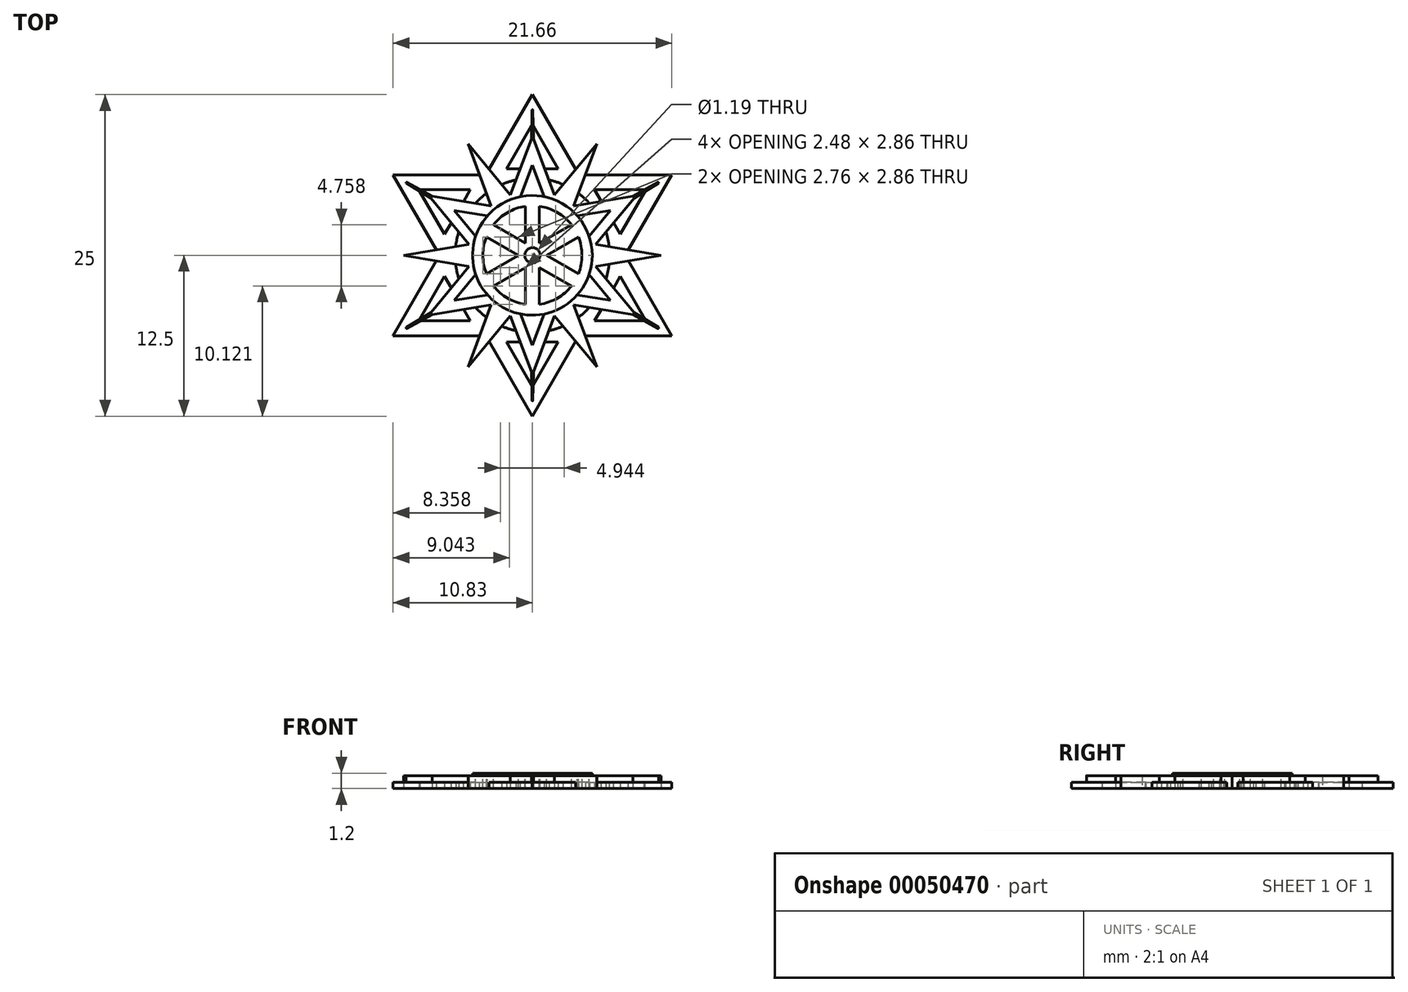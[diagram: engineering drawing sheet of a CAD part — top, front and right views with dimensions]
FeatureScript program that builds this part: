
annotation { "Feature Type Name" : "Feature", "Feature Type Description" : "" }
export const myFeature = defineFeature(function(context is Context, id is Id, definition is map)
    precondition{}
    {
        {
            var Q0;
            Q0=qCreatedBy(makeId("Top.planeOp"),FACE);
            var sketch = newSketch(context, id + "F0", { "sketchPlane" : qUnion([Q0])});
            skCircle(sketch, "E0", {"center": v(0, 0) * mm, "radius": 12.5 * mm, "construction": true});
            skLineSegment(sketch, "E1", {"start": v(0, 12.5) * mm, "end": v(-10.83, -6.25) * mm});
            skLineSegment(sketch, "E2", {"start": v(-10.83, -6.25) * mm, "end": v(10.83, -6.25) * mm});
            skLineSegment(sketch, "E3", {"start": v(10.83, -6.25) * mm, "end": v(0, 12.5) * mm});
            skLineSegment(sketch, "E4", {"start": v(-10.83, 6.25) * mm, "end": v(10.83, 6.25) * mm});
            skLineSegment(sketch, "E5", {"start": v(10.83, 6.25) * mm, "end": v(0, -12.5) * mm});
            skLineSegment(sketch, "E6", {"start": v(0, -12.5) * mm, "end": v(-10.83, 6.25) * mm});
            skCircle(sketch, "E7", {"center": v(0, 0) * mm, "radius": 6 * mm});
            skLineSegment(sketch, "E8", {"start": v(-2, 6.73) * mm, "end": v(2, 6.73) * mm});
            skLineSegment(sketch, "E9", {"start": v(2, 6.73) * mm, "end": v(0, 10.2) * mm});
            skLineSegment(sketch, "E10", {"start": v(0, 10.2) * mm, "end": v(-2, 6.73) * mm});
            skLineSegment(sketch, "E11", {"start": v(0, 10.2) * mm, "end": v(0, 12.5) * mm, "construction": true});
            skLineSegment(sketch, "E12.1.0", {"start": v(-4.83, 5.1) * mm, "end": v(-8.83, 5.1) * mm});
            skLineSegment(sketch, "E12.1.1", {"start": v(-6.83, 1.63) * mm, "end": v(-4.83, 5.1) * mm});
            skLineSegment(sketch, "E12.1.2", {"start": v(-8.83, 5.1) * mm, "end": v(-6.83, 1.63) * mm});
            skLineSegment(sketch, "E12.2.0", {"start": v(-6.83, -1.63) * mm, "end": v(-8.83, -5.1) * mm});
            skLineSegment(sketch, "E12.2.1", {"start": v(-4.83, -5.1) * mm, "end": v(-6.83, -1.63) * mm});
            skLineSegment(sketch, "E12.2.2", {"start": v(-8.83, -5.1) * mm, "end": v(-4.83, -5.1) * mm});
            skLineSegment(sketch, "E12.3.0", {"start": v(-2, -6.73) * mm, "end": v(0, -10.2) * mm});
            skLineSegment(sketch, "E12.3.1", {"start": v(2, -6.73) * mm, "end": v(-2, -6.73) * mm});
            skLineSegment(sketch, "E12.3.2", {"start": v(0, -10.2) * mm, "end": v(2, -6.73) * mm});
            skLineSegment(sketch, "E12.4.0", {"start": v(4.83, -5.1) * mm, "end": v(8.83, -5.1) * mm});
            skLineSegment(sketch, "E12.4.1", {"start": v(6.83, -1.63) * mm, "end": v(4.83, -5.1) * mm});
            skLineSegment(sketch, "E12.4.2", {"start": v(8.83, -5.1) * mm, "end": v(6.83, -1.63) * mm});
            skLineSegment(sketch, "E12.5.0", {"start": v(6.83, 1.63) * mm, "end": v(8.83, 5.1) * mm});
            skLineSegment(sketch, "E12.5.1", {"start": v(4.83, 5.1) * mm, "end": v(6.83, 1.63) * mm});
            skLineSegment(sketch, "E12.5.2", {"start": v(8.83, 5.1) * mm, "end": v(4.83, 5.1) * mm});
            skSolve(sketch);
        }
        {
            var Q0;
            Q0=qSketchRegion(id+"F0",true);
            extrude(context, id + "F1", {"entities" : qUnion([Q0]), "depth" : .5 * mm});
        }
        {
            var Q0;
            Q0=qCreatedBy(makeId("Top.planeOp"),FACE);
            var sketch = newSketch(context, id + "F2", { "sketchPlane" : qUnion([Q0])});
            skArc(sketch, "E13", {"start": v(-1.72, 4.7) * mm, "mid": v(-2.5, 4.33) * mm, "end": v(-3.2, 3.84) * mm});
            skLineSegment(sketch, "E14", {"start": v(-1.72, 4.7) * mm, "end": v(-0.08, 9.05) * mm});
            skLineSegment(sketch, "E15", {"start": v(0.08, 9.05) * mm, "end": v(1.72, 4.7) * mm});
            skLineSegment(sketch, "E16", {"start": v(-0.08, 9.05) * mm, "end": v(-0.04, 11.28) * mm});
            skLineSegment(sketch, "E17", {"start": v(0.04, 11.28) * mm, "end": v(0.08, 9.05) * mm});
            skPoint(sketch, "E18.visualSharp", {"position": v(0, 13.28) * mm});
            skArc(sketch, "E18.filletArc", {"start": v(0.04, 11.28) * mm, "mid": v(0, 11.32) * mm, "end": v(-0.04, 11.28) * mm});
            skPoint(sketch, "E19.orphan", {"position": v(0, 9.28) * mm});
            skLineSegment(sketch, "E20.1.0", {"start": v(-4.93, 0.86) * mm, "end": v(-7.88, 4.45) * mm});
            skLineSegment(sketch, "E20.1.1", {"start": v(-7.88, 4.45) * mm, "end": v(-9.79, 5.6) * mm});
            skLineSegment(sketch, "E20.1.2", {"start": v(-9.75, 5.67) * mm, "end": v(-7.8, 4.6) * mm});
            skLineSegment(sketch, "E20.1.3", {"start": v(-7.8, 4.6) * mm, "end": v(-3.2, 3.84) * mm});
            skArc(sketch, "E20.1.4", {"start": v(-9.75, 5.67) * mm, "mid": v(-9.8, 5.66) * mm, "end": v(-9.79, 5.6) * mm});
            skLineSegment(sketch, "E20.2.0", {"start": v(-3.2, -3.84) * mm, "end": v(-7.8, -4.6) * mm});
            skLineSegment(sketch, "E20.2.1", {"start": v(-7.8, -4.6) * mm, "end": v(-9.75, -5.67) * mm});
            skLineSegment(sketch, "E20.2.2", {"start": v(-9.79, -5.6) * mm, "end": v(-7.88, -4.45) * mm});
            skLineSegment(sketch, "E20.2.3", {"start": v(-7.88, -4.45) * mm, "end": v(-4.93, -0.86) * mm});
            skArc(sketch, "E20.2.4", {"start": v(-9.79, -5.6) * mm, "mid": v(-9.8, -5.66) * mm, "end": v(-9.75, -5.67) * mm});
            skLineSegment(sketch, "E20.3.0", {"start": v(1.72, -4.7) * mm, "end": v(0.08, -9.05) * mm});
            skLineSegment(sketch, "E20.3.1", {"start": v(0.08, -9.05) * mm, "end": v(0.04, -11.28) * mm});
            skLineSegment(sketch, "E20.3.2", {"start": v(-0.04, -11.28) * mm, "end": v(-0.08, -9.05) * mm});
            skLineSegment(sketch, "E20.3.3", {"start": v(-0.08, -9.05) * mm, "end": v(-1.72, -4.7) * mm});
            skArc(sketch, "E20.3.4", {"start": v(-0.04, -11.28) * mm, "mid": v(0, -11.32) * mm, "end": v(0.04, -11.28) * mm});
            skLineSegment(sketch, "E20.4.0", {"start": v(4.93, -0.86) * mm, "end": v(7.88, -4.45) * mm});
            skLineSegment(sketch, "E20.4.1", {"start": v(7.88, -4.45) * mm, "end": v(9.79, -5.6) * mm});
            skLineSegment(sketch, "E20.4.2", {"start": v(9.75, -5.67) * mm, "end": v(7.8, -4.6) * mm});
            skLineSegment(sketch, "E20.4.3", {"start": v(7.8, -4.6) * mm, "end": v(3.2, -3.84) * mm});
            skArc(sketch, "E20.4.4", {"start": v(9.75, -5.67) * mm, "mid": v(9.8, -5.66) * mm, "end": v(9.79, -5.6) * mm});
            skLineSegment(sketch, "E20.5.0", {"start": v(3.2, 3.84) * mm, "end": v(7.8, 4.6) * mm});
            skLineSegment(sketch, "E20.5.1", {"start": v(7.8, 4.6) * mm, "end": v(9.75, 5.67) * mm});
            skLineSegment(sketch, "E20.5.2", {"start": v(9.79, 5.6) * mm, "end": v(7.88, 4.45) * mm});
            skLineSegment(sketch, "E20.5.3", {"start": v(7.88, 4.45) * mm, "end": v(4.93, 0.86) * mm});
            skArc(sketch, "E20.5.4", {"start": v(9.79, 5.6) * mm, "mid": v(9.8, 5.66) * mm, "end": v(9.75, 5.67) * mm});
            skArc(sketch, "E21.trimOffspring", {"start": v(3.2, 3.84) * mm, "mid": v(2.5, 4.33) * mm, "end": v(1.72, 4.7) * mm});
            skArc(sketch, "E22.trimOffspring", {"start": v(-4.93, 0.86) * mm, "mid": v(-5, 0) * mm, "end": v(-4.93, -0.86) * mm});
            skArc(sketch, "E23.trimOffspring", {"start": v(4.93, -0.86) * mm, "mid": v(5, 0) * mm, "end": v(4.93, 0.86) * mm});
            skArc(sketch, "E24.trimOffspring", {"start": v(1.72, -4.7) * mm, "mid": v(2.5, -4.33) * mm, "end": v(3.2, -3.84) * mm});
            skArc(sketch, "E25.trimOffspring", {"start": v(-3.2, -3.84) * mm, "mid": v(-2.5, -4.33) * mm, "end": v(-1.72, -4.7) * mm});
            skLineSegment(sketch, "E26", {"start": v(0, 7) * mm, "end": v(0.75, 5) * mm});
            skLineSegment(sketch, "E27", {"start": v(0.75, 5) * mm, "end": v(-0.75, 5) * mm});
            skLineSegment(sketch, "E28", {"start": v(-0.75, 5) * mm, "end": v(0, 7) * mm});
            skLineSegment(sketch, "E29.1.0", {"start": v(-4.7, 1.85) * mm, "end": v(-6.06, 3.5) * mm});
            skLineSegment(sketch, "E29.1.1", {"start": v(-6.06, 3.5) * mm, "end": v(-3.96, 3.15) * mm});
            skLineSegment(sketch, "E29.1.2", {"start": v(-3.96, 3.15) * mm, "end": v(-4.7, 1.85) * mm});
            skLineSegment(sketch, "E29.2.0", {"start": v(-3.96, -3.15) * mm, "end": v(-6.06, -3.5) * mm});
            skLineSegment(sketch, "E29.2.1", {"start": v(-6.06, -3.5) * mm, "end": v(-4.7, -1.85) * mm});
            skLineSegment(sketch, "E29.2.2", {"start": v(-4.7, -1.85) * mm, "end": v(-3.96, -3.15) * mm});
            skLineSegment(sketch, "E29.3.0", {"start": v(0.75, -5) * mm, "end": v(0, -7) * mm});
            skLineSegment(sketch, "E29.3.1", {"start": v(0, -7) * mm, "end": v(-0.75, -5) * mm});
            skLineSegment(sketch, "E29.3.2", {"start": v(-0.75, -5) * mm, "end": v(0.75, -5) * mm});
            skLineSegment(sketch, "E29.4.0", {"start": v(4.7, -1.85) * mm, "end": v(6.06, -3.5) * mm});
            skLineSegment(sketch, "E29.4.1", {"start": v(6.06, -3.5) * mm, "end": v(3.96, -3.15) * mm});
            skLineSegment(sketch, "E29.4.2", {"start": v(3.96, -3.15) * mm, "end": v(4.7, -1.85) * mm});
            skLineSegment(sketch, "E29.5.0", {"start": v(3.96, 3.15) * mm, "end": v(6.06, 3.5) * mm});
            skLineSegment(sketch, "E29.5.1", {"start": v(6.06, 3.5) * mm, "end": v(4.7, 1.85) * mm});
            skLineSegment(sketch, "E29.5.2", {"start": v(4.7, 1.85) * mm, "end": v(3.96, 3.15) * mm});
            skLineSegment(sketch, "E30", {"start": v(0, 9.28) * mm, "end": v(0, 13.28) * mm, "construction": true});
            skLineSegment(sketch, "E31", {"start": v(-3.2, 3.84) * mm, "end": v(-5, 8.66) * mm});
            skLineSegment(sketch, "E32", {"start": v(-5, 8.66) * mm, "end": v(-1.72, 4.7) * mm});
            skLineSegment(sketch, "E33", {"start": v(-5, 8.66) * mm, "end": v(-2.5, 4.33) * mm, "construction": true});
            skLineSegment(sketch, "E34.1.0", {"start": v(-10, 0) * mm, "end": v(-4.93, 0.86) * mm});
            skLineSegment(sketch, "E34.1.1", {"start": v(-4.93, -0.86) * mm, "end": v(-10, 0) * mm});
            skLineSegment(sketch, "E34.2.0", {"start": v(-5, -8.66) * mm, "end": v(-3.2, -3.84) * mm});
            skLineSegment(sketch, "E34.2.1", {"start": v(-1.72, -4.7) * mm, "end": v(-5, -8.66) * mm});
            skLineSegment(sketch, "E34.3.0", {"start": v(5, -8.66) * mm, "end": v(1.72, -4.7) * mm});
            skLineSegment(sketch, "E34.3.1", {"start": v(3.2, -3.84) * mm, "end": v(5, -8.66) * mm});
            skLineSegment(sketch, "E34.4.0", {"start": v(10, 0) * mm, "end": v(4.93, -0.86) * mm});
            skLineSegment(sketch, "E34.4.1", {"start": v(4.93, 0.86) * mm, "end": v(10, 0) * mm});
            skLineSegment(sketch, "E34.5.0", {"start": v(5, 8.66) * mm, "end": v(3.2, 3.84) * mm});
            skLineSegment(sketch, "E34.5.1", {"start": v(1.72, 4.7) * mm, "end": v(5, 8.66) * mm});
            skSolve(sketch);
        }
        {
            var Q0;
            Q0=qSketchRegion(id+"F2",true);
            extrude(context, id + "F3", {"entities" : qUnion([Q0]), "operationType" : NewBodyOperationType.ADD, "depth" : 1 * mm});
        }
        {
            var Q0;
            Q0=makeQuery(id+"F3.opExtrude","CAP_FACE",FACE,{"disambiguationData":[OSD([sQuery(id+"F2.wireOp",EDGE,"E13"),sQuery(id+"F2.wireOp",EDGE,"E14"),sQuery(id+"F2.wireOp",EDGE,"E15"),sQuery(id+"F2.wireOp",EDGE,"E16"),sQuery(id+"F2.wireOp",EDGE,"E17"),sQuery(id+"F2.wireOp",EDGE,"E18.filletArc"),sQuery(id+"F2.wireOp",EDGE,"E20.1.0"),sQuery(id+"F2.wireOp",EDGE,"E20.1.1"),sQuery(id+"F2.wireOp",EDGE,"E20.1.2"),sQuery(id+"F2.wireOp",EDGE,"E20.1.3"),sQuery(id+"F2.wireOp",EDGE,"E20.1.4"),sQuery(id+"F2.wireOp",EDGE,"E20.2.0"),sQuery(id+"F2.wireOp",EDGE,"E20.2.1"),sQuery(id+"F2.wireOp",EDGE,"E20.2.2"),sQuery(id+"F2.wireOp",EDGE,"E20.2.3"),sQuery(id+"F2.wireOp",EDGE,"E20.2.4"),sQuery(id+"F2.wireOp",EDGE,"E20.3.0"),sQuery(id+"F2.wireOp",EDGE,"E20.3.1"),sQuery(id+"F2.wireOp",EDGE,"E20.3.2"),sQuery(id+"F2.wireOp",EDGE,"E20.3.3"),sQuery(id+"F2.wireOp",EDGE,"E20.3.4"),sQuery(id+"F2.wireOp",EDGE,"E20.4.0"),sQuery(id+"F2.wireOp",EDGE,"E20.4.1"),sQuery(id+"F2.wireOp",EDGE,"E20.4.2"),sQuery(id+"F2.wireOp",EDGE,"E20.4.3"),sQuery(id+"F2.wireOp",EDGE,"E20.4.4"),sQuery(id+"F2.wireOp",EDGE,"E20.5.0"),sQuery(id+"F2.wireOp",EDGE,"E20.5.1"),sQuery(id+"F2.wireOp",EDGE,"E20.5.2"),sQuery(id+"F2.wireOp",EDGE,"E20.5.3"),sQuery(id+"F2.wireOp",EDGE,"E20.5.4"),sQuery(id+"F2.wireOp",EDGE,"E21.trimOffspring"),sQuery(id+"F2.wireOp",EDGE,"E22.trimOffspring"),sQuery(id+"F2.wireOp",EDGE,"E23.trimOffspring"),sQuery(id+"F2.wireOp",EDGE,"E24.trimOffspring"),sQuery(id+"F2.wireOp",EDGE,"E25.trimOffspring"),sQuery(id+"F2.wireOp",EDGE,"E26"),sQuery(id+"F2.wireOp",EDGE,"E27"),sQuery(id+"F2.wireOp",EDGE,"E28"),sQuery(id+"F2.wireOp",EDGE,"E29.1.0"),sQuery(id+"F2.wireOp",EDGE,"E29.1.1"),sQuery(id+"F2.wireOp",EDGE,"E29.1.2"),sQuery(id+"F2.wireOp",EDGE,"E29.2.0"),sQuery(id+"F2.wireOp",EDGE,"E29.2.1"),sQuery(id+"F2.wireOp",EDGE,"E29.2.2"),sQuery(id+"F2.wireOp",EDGE,"E29.3.0"),sQuery(id+"F2.wireOp",EDGE,"E29.3.1"),sQuery(id+"F2.wireOp",EDGE,"E29.3.2"),sQuery(id+"F2.wireOp",EDGE,"E29.4.0"),sQuery(id+"F2.wireOp",EDGE,"E29.4.1"),sQuery(id+"F2.wireOp",EDGE,"E29.4.2"),sQuery(id+"F2.wireOp",EDGE,"E29.5.0"),sQuery(id+"F2.wireOp",EDGE,"E29.5.1"),sQuery(id+"F2.wireOp",EDGE,"E29.5.2")])],"isStart":false});
            var sketch = newSketch(context, id + "F4", { "sketchPlane" : qUnion([Q0])});
            skCircle(sketch, "E35", {"center": v(0, 0) * mm, "radius": 4.65 * mm});
            skSolve(sketch);
        }
        {
            var Q0;
            Q0=qSketchRegion(id+"F4",true);
            extrude(context, id + "F5", {"entities" : qUnion([Q0]), "operationType" : NewBodyOperationType.ADD, "depth" : .2 * mm, "hasSecondDirection" : true, "secondDirectionBound" : BoundingType.UP_TO_NEXT, "secondDirectionOppositeDirection" : true, "secondDirectionDepth" : 25 * mm});
        }
        {
            var Q0;
            Q0=makeQuery(id+"F5.opExtrude","CAP_FACE",FACE,{"disambiguationData":[OSD([sQuery(id+"F4.wireOp",EDGE,"E35")])],"isStart":false});
            var sketch = newSketch(context, id + "F6", { "sketchPlane" : qUnion([Q0])});
            skArc(sketch, "E36", {"start": v(-0.55, 3.81) * mm, "mid": v(-1.93, 3.33) * mm, "end": v(-3.03, 2.38) * mm});
            skLineSegment(sketch, "E37", {"start": v(-0.55, 3.81) * mm, "end": v(-0.55, 0.95) * mm});
            skLineSegment(sketch, "E38", {"start": v(0.55, 0.95) * mm, "end": v(0.55, 3.81) * mm});
            skLineSegment(sketch, "E39", {"start": v(3.85, 0) * mm, "end": v(0, 0) * mm, "construction": true});
            skLineSegment(sketch, "E40", {"start": v(0.55, 0.95) * mm, "end": v(0, 0) * mm, "construction": true});
            skLineSegment(sketch, "E41.1.0", {"start": v(-3.57, 1.43) * mm, "end": v(-1.1, 0) * mm});
            skLineSegment(sketch, "E41.1.1", {"start": v(-0.55, 0.95) * mm, "end": v(-3.03, 2.38) * mm});
            skLineSegment(sketch, "E41.2.0", {"start": v(-3.03, -2.38) * mm, "end": v(-0.55, -0.95) * mm});
            skLineSegment(sketch, "E41.2.1", {"start": v(-1.1, 0) * mm, "end": v(-3.57, -1.43) * mm});
            skLineSegment(sketch, "E41.3.0", {"start": v(0.55, -3.81) * mm, "end": v(0.55, -0.95) * mm});
            skLineSegment(sketch, "E41.3.1", {"start": v(-0.55, -0.95) * mm, "end": v(-0.55, -3.81) * mm});
            skLineSegment(sketch, "E41.4.0", {"start": v(3.57, -1.43) * mm, "end": v(1.1, 0) * mm});
            skLineSegment(sketch, "E41.4.1", {"start": v(0.55, -0.95) * mm, "end": v(3.03, -2.38) * mm});
            skLineSegment(sketch, "E41.5.0", {"start": v(3.03, 2.38) * mm, "end": v(0.55, 0.95) * mm});
            skLineSegment(sketch, "E41.5.1", {"start": v(1.1, 0) * mm, "end": v(3.57, 1.43) * mm});
            skArc(sketch, "E42.trimOffspring", {"start": v(-3.57, 1.43) * mm, "mid": v(-3.85, 0) * mm, "end": v(-3.57, -1.43) * mm});
            skArc(sketch, "E43.trimOffspring", {"start": v(-3.03, -2.38) * mm, "mid": v(-1.92, -3.33) * mm, "end": v(-0.55, -3.81) * mm});
            skArc(sketch, "E44.trimOffspring", {"start": v(0.55, -3.81) * mm, "mid": v(1.92, -3.33) * mm, "end": v(3.03, -2.38) * mm});
            skArc(sketch, "E45.trimOffspring", {"start": v(3.57, -1.43) * mm, "mid": v(3.85, 0) * mm, "end": v(3.57, 1.43) * mm});
            skArc(sketch, "E46.trimOffspring", {"start": v(3.03, 2.38) * mm, "mid": v(1.92, 3.33) * mm, "end": v(0.55, 3.81) * mm});
            skCircle(sketch, "E47", {"center": v(0, 0) * mm, "radius": 0.6 * mm});
            skSolve(sketch);
        }
        {
            var Q0;
            Q0=qSketchRegion(id+"F6",true);
            extrude(context, id + "F7", {"entities" : qUnion([Q0]), "operationType" : NewBodyOperationType.REMOVE, "endBound" : BoundingType.UP_TO_NEXT, "oppositeDirection" : true, "depth" : 25 * mm});
        }
        {
            var Q0;
            Q0=makeQuery(id+"F3.opExtrude","CAP_FACE",FACE,{"disambiguationData":[OSD([sQuery(id+"F2.wireOp",EDGE,"E13"),sQuery(id+"F2.wireOp",EDGE,"E14"),sQuery(id+"F2.wireOp",EDGE,"E15"),sQuery(id+"F2.wireOp",EDGE,"E16"),sQuery(id+"F2.wireOp",EDGE,"E17"),sQuery(id+"F2.wireOp",EDGE,"E18.filletArc"),sQuery(id+"F2.wireOp",EDGE,"E20.1.0"),sQuery(id+"F2.wireOp",EDGE,"E20.1.1"),sQuery(id+"F2.wireOp",EDGE,"E20.1.2"),sQuery(id+"F2.wireOp",EDGE,"E20.1.3"),sQuery(id+"F2.wireOp",EDGE,"E20.1.4"),sQuery(id+"F2.wireOp",EDGE,"E20.2.0"),sQuery(id+"F2.wireOp",EDGE,"E20.2.1"),sQuery(id+"F2.wireOp",EDGE,"E20.2.2"),sQuery(id+"F2.wireOp",EDGE,"E20.2.3"),sQuery(id+"F2.wireOp",EDGE,"E20.2.4"),sQuery(id+"F2.wireOp",EDGE,"E20.3.0"),sQuery(id+"F2.wireOp",EDGE,"E20.3.1"),sQuery(id+"F2.wireOp",EDGE,"E20.3.2"),sQuery(id+"F2.wireOp",EDGE,"E20.3.3"),sQuery(id+"F2.wireOp",EDGE,"E20.3.4"),sQuery(id+"F2.wireOp",EDGE,"E20.4.0"),sQuery(id+"F2.wireOp",EDGE,"E20.4.1"),sQuery(id+"F2.wireOp",EDGE,"E20.4.2"),sQuery(id+"F2.wireOp",EDGE,"E20.4.3"),sQuery(id+"F2.wireOp",EDGE,"E20.4.4"),sQuery(id+"F2.wireOp",EDGE,"E20.5.0"),sQuery(id+"F2.wireOp",EDGE,"E20.5.1"),sQuery(id+"F2.wireOp",EDGE,"E20.5.2"),sQuery(id+"F2.wireOp",EDGE,"E20.5.3"),sQuery(id+"F2.wireOp",EDGE,"E20.5.4"),sQuery(id+"F2.wireOp",EDGE,"E21.trimOffspring"),sQuery(id+"F2.wireOp",EDGE,"E22.trimOffspring"),sQuery(id+"F2.wireOp",EDGE,"E23.trimOffspring"),sQuery(id+"F2.wireOp",EDGE,"E24.trimOffspring"),sQuery(id+"F2.wireOp",EDGE,"E25.trimOffspring"),sQuery(id+"F2.wireOp",EDGE,"E26"),sQuery(id+"F2.wireOp",EDGE,"E27"),sQuery(id+"F2.wireOp",EDGE,"E28"),sQuery(id+"F2.wireOp",EDGE,"E29.1.0"),sQuery(id+"F2.wireOp",EDGE,"E29.1.1"),sQuery(id+"F2.wireOp",EDGE,"E29.1.2"),sQuery(id+"F2.wireOp",EDGE,"E29.2.0"),sQuery(id+"F2.wireOp",EDGE,"E29.2.1"),sQuery(id+"F2.wireOp",EDGE,"E29.2.2"),sQuery(id+"F2.wireOp",EDGE,"E29.3.0"),sQuery(id+"F2.wireOp",EDGE,"E29.3.1"),sQuery(id+"F2.wireOp",EDGE,"E29.3.2"),sQuery(id+"F2.wireOp",EDGE,"E29.4.0"),sQuery(id+"F2.wireOp",EDGE,"E29.4.1"),sQuery(id+"F2.wireOp",EDGE,"E29.4.2"),sQuery(id+"F2.wireOp",EDGE,"E29.5.0"),sQuery(id+"F2.wireOp",EDGE,"E29.5.1"),sQuery(id+"F2.wireOp",EDGE,"E29.5.2"),sQuery(id+"F2.wireOp",EDGE,"e1e6c283-0c3a-42df-8d1c-1fea8579a4a0"),sQuery(id+"F2.wireOp",EDGE,"f4f7e5aa-7f17-4f72-ba16-6a29db51923f"),sQuery(id+"F2.wireOp",EDGE,"981ffc64-7e8b-4a68-9272-58f16e235743.1.0"),sQuery(id+"F2.wireOp",EDGE,"981ffc64-7e8b-4a68-9272-58f16e235743.1.1"),sQuery(id+"F2.wireOp",EDGE,"981ffc64-7e8b-4a68-9272-58f16e235743.2.0"),sQuery(id+"F2.wireOp",EDGE,"981ffc64-7e8b-4a68-9272-58f16e235743.2.1"),sQuery(id+"F2.wireOp",EDGE,"981ffc64-7e8b-4a68-9272-58f16e235743.3.0"),sQuery(id+"F2.wireOp",EDGE,"981ffc64-7e8b-4a68-9272-58f16e235743.3.1"),sQuery(id+"F2.wireOp",EDGE,"981ffc64-7e8b-4a68-9272-58f16e235743.4.0"),sQuery(id+"F2.wireOp",EDGE,"981ffc64-7e8b-4a68-9272-58f16e235743.4.1"),sQuery(id+"F2.wireOp",EDGE,"981ffc64-7e8b-4a68-9272-58f16e235743.5.0"),sQuery(id+"F2.wireOp",EDGE,"981ffc64-7e8b-4a68-9272-58f16e235743.5.1")])],"isStart":false});
            var sketch = newSketch(context, id + "F8", { "sketchPlane" : qUnion([Q0])});
            skLineSegment(sketch, "E48.0", {"start": v(0, 7) * mm, "end": v(0.92, 4.56) * mm});
            skLineSegment(sketch, "E48.1", {"start": v(-0.92, 4.56) * mm, "end": v(0, 7) * mm});
            skArc(sketch, "E48.2", {"start": v(-3.5, 3.07) * mm, "mid": v(-4.03, 2.33) * mm, "end": v(-4.4, 1.49) * mm});
            skLineSegment(sketch, "E49.0", {"start": v(3.5, 3.07) * mm, "end": v(6.06, 3.5) * mm});
            skLineSegment(sketch, "E49.1", {"start": v(6.06, 3.5) * mm, "end": v(4.4, 1.49) * mm});
            skLineSegment(sketch, "E50.0", {"start": v(4.4, -1.49) * mm, "end": v(6.06, -3.5) * mm});
            skLineSegment(sketch, "E50.1", {"start": v(6.06, -3.5) * mm, "end": v(3.5, -3.07) * mm});
            skLineSegment(sketch, "E50.2", {"start": v(0.92, -4.56) * mm, "end": v(0, -7) * mm});
            skLineSegment(sketch, "E50.3", {"start": v(0, -7) * mm, "end": v(-0.92, -4.56) * mm});
            skLineSegment(sketch, "E50.4", {"start": v(-3.5, -3.07) * mm, "end": v(-6.06, -3.5) * mm});
            skLineSegment(sketch, "E50.5", {"start": v(-6.06, -3.5) * mm, "end": v(-4.4, -1.49) * mm});
            skLineSegment(sketch, "E50.6", {"start": v(-4.4, 1.49) * mm, "end": v(-6.06, 3.5) * mm});
            skLineSegment(sketch, "E50.7", {"start": v(-6.06, 3.5) * mm, "end": v(-3.5, 3.07) * mm});
            skArc(sketch, "E51.trimOffspring", {"start": v(0.92, 4.56) * mm, "mid": v(0, 4.65) * mm, "end": v(-0.92, 4.56) * mm});
            skArc(sketch, "E52.trimOffspring", {"start": v(4.4, 1.49) * mm, "mid": v(4.03, 2.33) * mm, "end": v(3.5, 3.07) * mm});
            skArc(sketch, "E53.trimOffspring", {"start": v(3.5, -3.07) * mm, "mid": v(4.03, -2.33) * mm, "end": v(4.4, -1.49) * mm});
            skArc(sketch, "E54.trimOffspring", {"start": v(-0.92, -4.56) * mm, "mid": v(0, -4.65) * mm, "end": v(0.92, -4.56) * mm});
            skArc(sketch, "E55.trimOffspring", {"start": v(-4.4, -1.49) * mm, "mid": v(-4.03, -2.32) * mm, "end": v(-3.5, -3.07) * mm});
            skSolve(sketch);
        }
        {
            var Q0;
            Q0=qSketchRegion(id+"F8",true);
            extrude(context, id + "F9", {"entities" : qUnion([Q0]), "operationType" : NewBodyOperationType.REMOVE, "endBound" : BoundingType.THROUGH_ALL, "oppositeDirection" : true, "depth" : 25 * mm});
        }
    });
